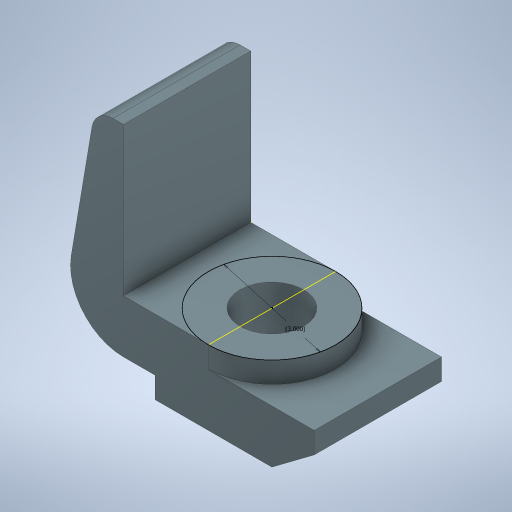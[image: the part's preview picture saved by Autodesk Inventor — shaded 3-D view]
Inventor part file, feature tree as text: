
AUTODESK INVENTOR PART (.ipt)
format: ipt  version: 2024 (Build 280153000, 153)  size: 291,328 bytes
history: native  units: in
note: dims shown in document units (in); Inventor stores cm internally (conversion verified against a paired STEP export)
features: extrude x2, other x2, hole x1, sketch x1
ambient origin geometry x8: Origin, YZ Plane, XZ Plane, XY Plane, X Axis, Y Axis, Z Axis, Center Point
bodies: Solid1 (feature_tree)
feature tree (6):
  extrude  "FULL EXTRUSION"  Depth=0.5in
  extrude  "Half Circle Extrusion"  Depth=0.5in
  hole  "Hole2"  [1 undecoded]
  other  "main profile"
  other  "Half Circle"
  sketch  "Sketch6"  dims[d8=2.0in d9=0.5in d11=2.75in d15=4.5in d16=0.5in d18=1.75in d20=0.75in d21=2.5in d23=3.0in d24=0.0in d41=0.5in d42=1.25in d44=1.25in d45=4.75in d46=1.0in d47=0.0in d48=1.5in d49=0.75in d50=0.375in d51=0.25in d52=0.5635in d53=1.0in d54=0.8108in d55=3.0in d56=0.25in d64=4.5in d57=0.5in d58=0.0344in]
note: 1 required parameter value undecoded (feature->parameter linkage not recoverable at this tier; creation-order binding heuristic only, values carry confidence <= 0.55)
